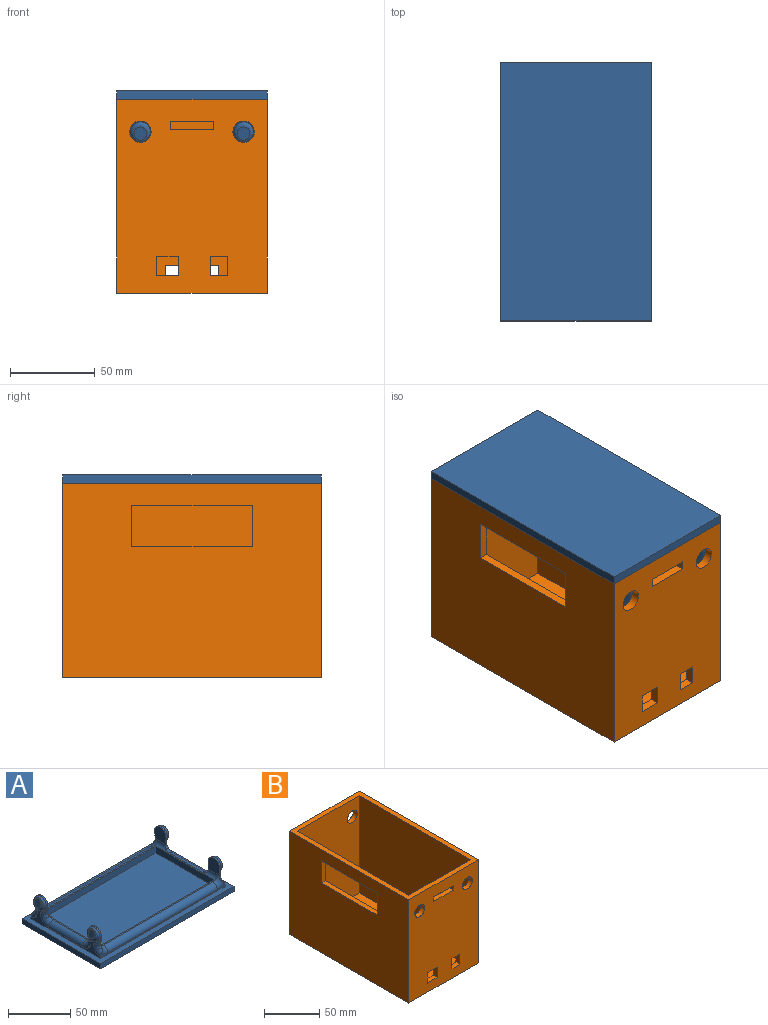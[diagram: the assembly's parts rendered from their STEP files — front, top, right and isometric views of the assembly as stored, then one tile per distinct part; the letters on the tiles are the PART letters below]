
ASSEMBLY  parts=2 mates=1
PART A: 107 faces, bbox 154.4x89.1x30.7 mm
  f0: plane 38.1x1.27mm, normal (0,0,1), area 48.4mm2, adj f12,f28,f30,f88
  f1: plane 124.41x1.27mm, normal (0,0,1), area 158mm2, adj f11,f27,f47,f102
  f2: plane 129.49x65.99mm, normal (0,0,1), area 8544.9mm2, adj f11,f12,f13,f34
  f3: plane 152.4x88.9mm, normal (0,0,1), area 2359.6mm2, adj f4,f5,f6,f8,f9,f10,f32,f33
  f4: plane 152.4x5.08mm, normal (0,1,0), area 774.2mm2, adj f3,f5,f7,f32
  f5: plane 88.9x5.08mm, normal (-1,0,0), area 451.6mm2, adj f3,f4,f6,f7
  f6: plane 152.4x5.08mm, normal (0,-1,0), area 774.2mm2, adj f3,f5,f7,f32
  f7: plane 152.4x88.9mm, normal (0,0,-1), area 13548.4mm2, adj f4,f5,f6,f32
  f8: plane 142.36x4.75mm, normal (0,1,0), area 201.8mm2, adj f3,f9,f33,f51,f76,f104,f105,f106
  f9: plane 78.71x13.39mm, normal (-1,0,0), area 241.6mm2, adj f3,f8,f10,f25,f26,f76,f77,f78
  f10: plane 142.36x4.75mm, normal (0,-1,0), area 201.8mm2, adj f3,f9,f33,f75,f100,f101,f102,f103
  f11: plane 129.49x7.03mm, normal (0,1,0), area 823.4mm2, adj f1,f2,f12,f27,f34,f47
  f12: plane 65.99x7.03mm, normal (1,0,0), area 435.7mm2, adj f0,f2,f11,f13,f27,f28,f29,f30
  f13: plane 129.49x7.03mm, normal (0,-1,0), area 823.4mm2, adj f2,f12,f14,f29,f34,f49
  f14: plane 124.41x1.27mm, normal (0,0,1), area 158mm2, adj f13,f29,f49,f105
  f15: plane 2.14x1.61mm, normal (0,-1,0), area 1.9mm2, adj f16,f18,f83
  f16: cylinder r=6.35mm len=12.7mm, axis (-1,0,0), area 32.2mm2, adj f15,f17,f18,f82
  f17: plane 2.14x1.61mm, normal (0,1,0), area 1.9mm2, adj f16,f18,f81
  f18: plane 14.19x12.92mm, normal (1,0,0), area 156.7mm2, adj f15,f16,f17,f29,f80,f84,f85,f104
  f19: plane 2.14x1.61mm, normal (0,-1,0), area 1.9mm2, adj f20,f22,f95
  f20: cylinder r=6.35mm len=12.7mm, axis (-1,0,0), area 32.2mm2, adj f19,f21,f22,f94
  f21: plane 2.14x1.61mm, normal (0,1,0), area 1.9mm2, adj f20,f22,f93
  f22: plane 14.19x12.92mm, normal (1,0,0), area 156.7mm2, adj f19,f20,f21,f27,f91,f92,f96,f101
  f23: plane 8.01x7.34mm, normal (-0.98,0,0.21), area 46.8mm2, adj f26
  f24: plane 8.01x7.34mm, normal (-0.98,0,0.21), area 46.8mm2, adj f25
  f25: bspline ~11.7x11.69mm, area 79mm2, adj f9,f24,f92,f93,f94,f95,f96
  f26: bspline ~11.7x11.69mm, area 79mm2, adj f9,f23,f80,f81,f82,f83,f84
  f27: cylinder r=5.08mm len=12.67mm, axis (0,-1,0), area 62.8mm2, adj f1,f11,f12,f22,f28,f90,f101
  f28: cylinder r=5.08mm len=3.81mm, axis (1,0,0), area 4.4mm2, adj f0,f12,f27,f89
  f29: cylinder r=5.08mm len=12.67mm, axis (0,-1,0), area 62.8mm2, adj f12,f13,f14,f18,f30,f86,f104
  f30: cylinder r=5.08mm len=3.81mm, axis (-1,0,0), area 4.4mm2, adj f0,f12,f29,f87
  f31: plane 38.1x1.27mm, normal (0,0,1), area 48.4mm2, adj f34,f48,f50,f63
  f32: plane 88.9x5.08mm, normal (1,0,0), area 451.6mm2, adj f3,f4,f6,f7
  f33: plane 78.71x13.39mm, normal (1,0,0), area 241.6mm2, adj f3,f8,f10,f45,f46,f51,f52,f53
  f34: plane 65.99x7.03mm, normal (-1,0,0), area 435.7mm2, adj f2,f11,f13,f31,f47,f48,f49,f50
  f35: plane 2.14x1.61mm, normal (0,-1,0), area 1.9mm2, adj f36,f38,f58
  f36: cylinder r=6.35mm len=12.7mm, axis (1,0,0), area 32.2mm2, adj f35,f37,f38,f57
  f37: plane 2.14x1.61mm, normal (0,1,0), area 1.9mm2, adj f36,f38,f56
  f38: plane 14.19x12.92mm, normal (-1,0,0), area 156.7mm2, adj f35,f36,f37,f49,f55,f59,f60,f106
  f39: plane 2.14x1.61mm, normal (0,-1,0), area 1.9mm2, adj f40,f42,f70
  f40: cylinder r=6.35mm len=12.7mm, axis (1,0,0), area 32.2mm2, adj f39,f41,f42,f69
  f41: plane 2.14x1.61mm, normal (0,1,0), area 1.9mm2, adj f40,f42,f68
  f42: plane 14.19x12.92mm, normal (-1,0,0), area 156.7mm2, adj f39,f40,f41,f47,f66,f67,f71,f103
  f43: plane 8.01x7.34mm, normal (0.98,0,0.21), area 46.8mm2, adj f46
  f44: plane 8.01x7.34mm, normal (0.98,0,0.21), area 46.8mm2, adj f45
  f45: bspline ~11.7x11.69mm, area 79mm2, adj f33,f44,f67,f68,f69,f70,f71
  f46: bspline ~11.7x11.69mm, area 79mm2, adj f33,f43,f55,f56,f57,f58,f59
  f47: cylinder r=5.08mm len=12.67mm, axis (0,-1,0), area 62.8mm2, adj f1,f11,f34,f42,f48,f65,f103
  f48: cylinder r=5.08mm len=3.81mm, axis (-1,0,0), area 4.4mm2, adj f31,f34,f47,f64
  f49: cylinder r=5.08mm len=12.67mm, axis (0,-1,0), area 62.8mm2, adj f13,f14,f34,f38,f50,f61,f106
  f50: cylinder r=5.08mm len=3.81mm, axis (1,0,0), area 4.4mm2, adj f31,f34,f49,f62
  f51: torus R=10.16mm, axis (-1,0,0), area 30.3mm2, adj f8,f33,f52,f106
  f52: bspline ~7.06x6.38mm, area 25.9mm2, adj f33,f51,f53,f106
  f53: bspline ~5.03x4.48mm, area 3.8mm2, adj f33,f52,f54,f106
  f54: cylinder r=5.08mm len=4.83mm, axis (0,0,-1), area 12.1mm2, adj f33,f53,f55,f106
  f55: bspline ~4.92x3.81mm, area 10.1mm2, adj f38,f46,f54,f56,f106
  f56: bspline ~5.6x3.92mm, area 13.3mm2, adj f37,f46,f55,f57
  f57: torus R=1.27mm, axis (1,0,0), area 44.1mm2, adj f36,f46,f56,f58
  f58: bspline ~5.6x3.92mm, area 13.3mm2, adj f35,f46,f57,f59
  f59: bspline ~4.92x3.81mm, area 10.2mm2, adj f38,f46,f58,f60
  f60: cylinder r=5.08mm len=4.92mm, axis (0,0,-1), area 13mm2, adj f33,f38,f59,f61
  f61: bspline ~8.21x6.6mm, area 36.4mm2, adj f33,f49,f60,f62
  f62: torus R=10.16mm, axis (-1,0,0), area 46.9mm2, adj f33,f50,f61,f63
  f63: cylinder r=5.08mm len=38.1mm, axis (0,1,0), area 304mm2, adj f31,f33,f62,f64
  f64: torus R=10.16mm, axis (-1,0,0), area 46.9mm2, adj f33,f48,f63,f65
  f65: bspline ~8.63x6.71mm, area 36.4mm2, adj f33,f47,f64,f66
  f66: cylinder r=5.08mm len=4.92mm, axis (0,0,-1), area 13mm2, adj f33,f42,f65,f67
  f67: bspline ~4.92x3.81mm, area 10.2mm2, adj f42,f45,f66,f68
  f68: bspline ~5.6x3.92mm, area 13.3mm2, adj f41,f45,f67,f69
  f69: torus R=1.27mm, axis (1,0,0), area 44.1mm2, adj f40,f45,f68,f70
  f70: bspline ~5.6x3.92mm, area 13.3mm2, adj f39,f45,f69,f71
  f71: bspline ~4.92x3.81mm, area 10.1mm2, adj f42,f45,f70,f72,f103
  f72: cylinder r=5.08mm len=4.83mm, axis (0,0,-1), area 12.1mm2, adj f33,f71,f73,f103
  f73: bspline ~4.97x4.07mm, area 3.8mm2, adj f33,f72,f74,f103
  f74: bspline ~8x6.45mm, area 25.9mm2, adj f33,f73,f75,f103
  f75: torus R=10.16mm, axis (-1,0,0), area 30.3mm2, adj f10,f33,f74,f103
  f76: torus R=10.16mm, axis (1,0,0), area 30.3mm2, adj f8,f9,f77,f104
  f77: bspline ~8x6.45mm, area 25.9mm2, adj f9,f76,f78,f104
  f78: bspline ~4.97x4.07mm, area 3.8mm2, adj f9,f77,f79,f104
  f79: cylinder r=5.08mm len=4.83mm, axis (0,0,1), area 12.1mm2, adj f9,f78,f80,f104
  f80: bspline ~4.92x3.81mm, area 10.1mm2, adj f18,f26,f79,f81,f104
  f81: bspline ~5.54x3.92mm, area 13.3mm2, adj f17,f26,f80,f82
  f82: torus R=1.27mm, axis (-1,0,0), area 44.1mm2, adj f16,f26,f81,f83
  f83: bspline ~5.54x3.92mm, area 13.3mm2, adj f15,f26,f82,f84
  f84: bspline ~4.92x3.81mm, area 10.2mm2, adj f18,f26,f83,f85
  f85: cylinder r=5.08mm len=4.92mm, axis (0,0,1), area 13mm2, adj f9,f18,f84,f86
  f86: bspline ~8.44x6.6mm, area 36.4mm2, adj f9,f29,f85,f87
  f87: torus R=10.16mm, axis (1,0,0), area 46.9mm2, adj f9,f30,f86,f88
  f88: cylinder r=5.08mm len=38.1mm, axis (0,1,0), area 304mm2, adj f0,f9,f87,f89
  f89: torus R=10.16mm, axis (1,0,0), area 46.9mm2, adj f9,f28,f88,f90
  f90: bspline ~8.02x6.48mm, area 36.4mm2, adj f9,f27,f89,f91
  f91: cylinder r=5.08mm len=4.92mm, axis (0,0,1), area 13mm2, adj f9,f22,f90,f92
  f92: bspline ~4.92x3.81mm, area 10.2mm2, adj f22,f25,f91,f93
  f93: bspline ~5.54x3.92mm, area 13.3mm2, adj f21,f25,f92,f94
  f94: torus R=1.27mm, axis (-1,0,0), area 44.1mm2, adj f20,f25,f93,f95
  f95: bspline ~5.54x3.92mm, area 13.3mm2, adj f19,f25,f94,f96
  f96: bspline ~4.92x3.81mm, area 10.1mm2, adj f22,f25,f95,f97,f101
  f97: cylinder r=5.08mm len=4.83mm, axis (0,0,1), area 12.1mm2, adj f9,f96,f98,f101
  f98: bspline ~5.03x4.48mm, area 3.8mm2, adj f9,f97,f99,f101
  f99: bspline ~7x6.35mm, area 25.9mm2, adj f9,f98,f100,f101
  f100: torus R=10.16mm, axis (1,0,0), area 30.3mm2, adj f9,f10,f99,f101
  f101: torus R=10.16mm, axis (0,-1,0), area 61.8mm2, adj f10,f22,f27,f96,f97,f98,f99,f100
  f102: cylinder r=5.08mm len=124.41mm, axis (-1,0,0), area 992.7mm2, adj f1,f10,f101,f103
  f103: torus R=10.16mm, axis (0,-1,0), area 61.8mm2, adj f10,f42,f47,f71,f72,f73,f74,f75
  f104: torus R=10.16mm, axis (0,-1,0), area 61.8mm2, adj f8,f18,f29,f76,f77,f78,f79,f80
  f105: cylinder r=5.08mm len=124.41mm, axis (1,0,0), area 992.7mm2, adj f8,f14,f104,f106
  f106: torus R=10.16mm, axis (0,-1,0), area 61.8mm2, adj f8,f38,f49,f51,f52,f53,f54,f55
PART B: 43 faces, bbox 88.9x152.4x114.3 mm
  f0: plane 152.4x114.3mm, normal (1,0,0), area 17290.3mm2, adj f2,f4,f5,f6,f31,f32,f33,f34
  f1: plane 142.24x107.95mm, normal (-1,0,0), area 15225.8mm2, adj f3,f4,f8,f10,f31,f32,f33,f34
  f2: plane 114.3x88.9mm, normal (0,-1,0), area 9517.6mm2, adj f0,f4,f6,f7,f11,f12,f13,f14
  f3: plane 107.95x78.74mm, normal (0,1,0), area 7856.3mm2, adj f1,f4,f9,f10,f11,f12,f13,f14
  f4: plane 152.4x88.9mm, normal (0,0,1), area 2348.4mm2, adj f0,f1,f2,f3,f5,f7,f8,f9
  f5: plane 114.3x88.9mm, normal (0,1,0), area 9706.3mm2, adj f0,f4,f6,f7,f27,f28,f29,f30
  f6: plane 152.4x88.9mm, normal (0,0,-1), area 13548.4mm2, adj f0,f2,f5,f7
  f7: plane 152.4x114.3mm, normal (-1,0,0), area 15685.1mm2, adj f2,f4,f5,f6,f23,f24,f25,f26
  f8: plane 107.95x78.74mm, normal (0,-1,0), area 8045mm2, adj f1,f4,f9,f10,f27,f28,f29,f30
  f9: plane 142.24x107.95mm, normal (1,0,0), area 13620.6mm2, adj f3,f4,f8,f10,f23,f24,f25,f26
  f10: plane 142.24x78.74mm, normal (0,0,1), area 11200mm2, adj f1,f3,f8,f9
  f11: plane 11.43x5.08mm, normal (-1,0,0), area 58.1mm2, adj f2,f3,f12,f14
  f12: plane 12.7x5.08mm, normal (0,0,-1), area 64.5mm2, adj f2,f3,f11,f13
  f13: plane 11.43x5.08mm, normal (1,0,0), area 58.1mm2, adj f2,f3,f12,f14
  f14: plane 12.7x5.08mm, normal (0,0,1), area 64.5mm2, adj f2,f3,f11,f13
  f15: plane 10.16x5.08mm, normal (0,0,1), area 51.6mm2, adj f2,f3,f16,f18
  f16: plane 11.43x5.08mm, normal (-1,0,0), area 58.1mm2, adj f2,f3,f15,f17
  f17: plane 10.16x5.08mm, normal (0,0,-1), area 51.6mm2, adj f2,f3,f16,f18
  f18: plane 11.43x5.08mm, normal (1,0,0), area 58.1mm2, adj f2,f3,f15,f17
  f19: plane 25.4x5.08mm, normal (0,0,-1), area 129mm2, adj f2,f3,f20,f22
  f20: plane 5.08x5.08mm, normal (1,0,0), area 25.8mm2, adj f2,f3,f19,f21
  f21: plane 25.4x5.08mm, normal (0,0,1), area 129mm2, adj f2,f3,f20,f22
  f22: plane 5.08x5.08mm, normal (-1,0,0), area 25.8mm2, adj f2,f3,f19,f21
  f23: plane 71.12x5.08mm, normal (0,0,-1), area 361.3mm2, adj f7,f9,f24,f25
  f24: plane 24.38x5.08mm, normal (0,1,0), area 123.9mm2, adj f7,f9,f23,f26
  f25: plane 24.38x5.08mm, normal (0,-1,0), area 123.9mm2, adj f7,f9,f23,f26
  f26: plane 71.12x5.08mm, normal (0,0,1), area 361.3mm2, adj f7,f9,f24,f25
  f27: plane 6.35x5.08mm, normal (-1,0,0), area 32.3mm2, adj f5,f8,f28,f29
  f28: plane 31.75x5.08mm, normal (0,0,-1), area 161.3mm2, adj f5,f8,f27,f30
  f29: plane 31.75x5.08mm, normal (0,0,1), area 161.3mm2, adj f5,f8,f27,f30
  f30: plane 6.35x5.08mm, normal (1,0,0), area 32.3mm2, adj f5,f8,f28,f29
  f31: plane 12.7x5.08mm, normal (0,0,-1), area 64.5mm2, adj f0,f1,f32,f34
  f32: plane 5.08x5.08mm, normal (0,1,0), area 25.8mm2, adj f0,f1,f31,f33
  f33: plane 12.7x5.08mm, normal (0,0,1), area 64.5mm2, adj f0,f1,f32,f34
  f34: plane 5.08x5.08mm, normal (0,-1,0), area 25.8mm2, adj f0,f1,f31,f33
  f35: plane 12.7x5.08mm, normal (0,0,-1), area 64.5mm2, adj f0,f1,f36,f38
  f36: plane 5.08x5.08mm, normal (0,1,0), area 25.8mm2, adj f0,f1,f35,f37
  f37: plane 12.7x5.08mm, normal (0,0,1), area 64.5mm2, adj f0,f1,f36,f38
  f38: plane 5.08x5.08mm, normal (0,-1,0), area 25.8mm2, adj f0,f1,f35,f37
  f39: cylinder r=6.35mm len=12.7mm, axis (0,-1,0), area 202.7mm2, adj f5,f8
  f40: cylinder r=6.35mm len=12.7mm, axis (0,-1,0), area 202.7mm2, adj f5,f8
  f41: cylinder r=6.35mm len=12.7mm, axis (0,-1,0), area 202.7mm2, adj f2,f3
  f42: cylinder r=6.35mm len=12.7mm, axis (0,-1,0), area 202.7mm2, adj f2,f3
PLACE A rot(axis=(-0.71,0.71,0),180deg) t=(47.13,10.1,68.36)mm
PLACE B t=(47.13,10.1,6.13)mm
MATE planar B.f4 <-> A.f2  axis (0,0,1) through (47.13,10.1,63.28)mm
